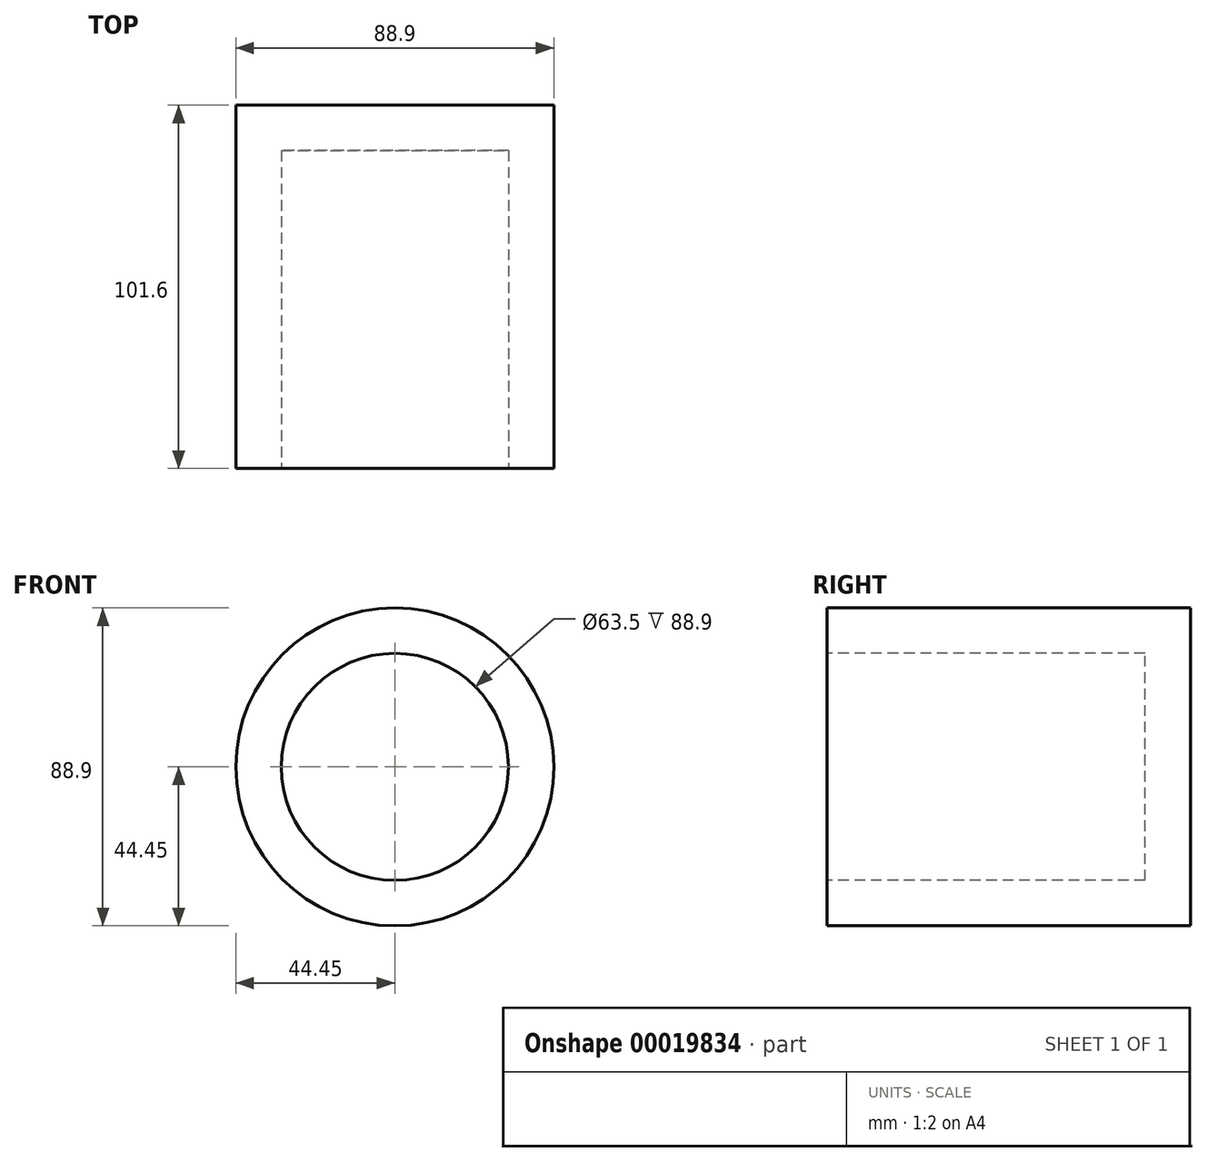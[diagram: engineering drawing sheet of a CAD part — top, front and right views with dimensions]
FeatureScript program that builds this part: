
annotation { "Feature Type Name" : "Feature", "Feature Type Description" : "" }
export const myFeature = defineFeature(function(context is Context, id is Id, definition is map)
    precondition{}
    {
        {
            var Q0;
            Q0=qCreatedBy(makeId("Front.planeOp"),FACE);
            var sketch = newSketch(context, id + "F0", { "sketchPlane" : qUnion([Q0])});
            skCircle(sketch, "E0", {"center": v(0, 0) * mm, "radius": 31.75 * mm});
            skSolve(sketch);
        }
        {
            var Q0;
            Q0=makeQuery(id+"F0.imprint","IMPRINT",FACE,{"disambiguationData":[TD([[makeQuery(id+"F0.imprint","IMPRINT",EDGE,{"derivedFrom":sQuery(id+"F0.wireOp",EDGE,"E0")}),1.0]])]});
            extrude(context, id + "F1", {"entities" : qUnion([Q0]), "oppositeDirection" : true, "depth" : 88.9 * mm});
        }
        {
            var Q0;
            Q0=makeQuery(id+"F1.opExtrude","CAP_FACE",FACE,{"disambiguationData":[OSD([sQuery(id+"F0.wireOp",EDGE,"E0")])],"isStart":true});
            var Q1;
            Q1=makeQuery(id+"F1.opExtrude","SWEPT_BODY",BODY,{"disambiguationData":[OSD([sQuery(id+"F0.wireOp",EDGE,"E0")])]});
            shell(context, id + "F2", {"entities" : qUnion([Q0]), "parts" : qUnion([Q1]), "thickness" : 12.7 * mm, "oppositeDirection" : true});
        }
    });
